FREECAD ASSEMBLY — COMPONENT RECIPES ("70_drawer_box_assembly")

This assembly document has 9 components, labeled P0..P8 below (a component is one placed body or linked part). 0 of them carry a construction recipe — the FreeCAD feature program that regenerates the part from scratch, quoted from this document or its linked companion documents; the rest are supplied as boundary geometry only. No exploded tour is included for this assembly.
COMPONENT P0 — geometry summary ("Body"; no construction recipe available for this part):
  bounding box: 525.0 x 393.0 x 18.0 mm
  tessellated surface: 28 triangles
  volume: 3690964 mm^3 (99% of its bounding box)
  symmetry: mirror-symmetric across its x mid-plane, z mid-plane
COMPONENT P1 — geometry summary ("Body003"; no construction recipe available for this part):
  bounding box: 525.0 x 393.0 x 18.0 mm
  tessellated surface: 28 triangles
  volume: 3690964 mm^3 (99% of its bounding box)
  symmetry: mirror-symmetric across its x mid-plane, z mid-plane
COMPONENT P2 — geometry summary ("Body004"; no construction recipe available for this part):
  bounding box: 771.0 x 378.0 x 18.0 mm
  tessellated surface: 8,124 triangles
  volume: 5203028 mm^3 (99% of its bounding box)
  symmetry: 2-fold rotationally symmetric about the y axis; mirror-symmetric across its x mid-plane
COMPONENT P3 — geometry summary ("Body005"; no construction recipe available for this part):
  bounding box: 771.0 x 378.0 x 18.0 mm
  tessellated surface: 8,124 triangles
  volume: 5203028 mm^3 (99% of its bounding box)
  symmetry: 2-fold rotationally symmetric about the y axis; mirror-symmetric across its x mid-plane
COMPONENT P4 — geometry summary ("Body007"; no construction recipe available for this part):
  bounding box: 489.0 x 101.0 x 18.0 mm
  tessellated surface: 44 triangles
  volume: 844503 mm^3 (95% of its bounding box)
  symmetry: 2-fold rotationally symmetric about the x axis; 2-fold rotationally symmetric about the y axis; 2-fold rotationally symmetric about the z axis; mirror-symmetric across its y mid-plane
COMPONENT P5 — geometry summary ("KV1-45-H45-L...-SC"; no construction recipe available for this part):
  bounding box: 350.0 x 45.0 x 12.7 mm
  tessellated surface: 10,296 triangles
  volume: 86644 mm^3 (43% of its bounding box)
  symmetry: mirror-symmetric across its z mid-plane
COMPONENT P6 — geometry summary ("KV1-45-H45-L...-SC001"; no construction recipe available for this part):
  bounding box: 350.0 x 45.0 x 12.7 mm
  tessellated surface: 10,296 triangles
  volume: 86644 mm^3 (43% of its bounding box)
  symmetry: mirror-symmetric across its z mid-plane
COMPONENT P7 — geometry summary ("KV1-45-H45-L...-SC002"; no construction recipe available for this part):
  bounding box: 350.0 x 45.0 x 12.7 mm
  tessellated surface: 10,296 triangles
  volume: 86644 mm^3 (43% of its bounding box)
  symmetry: mirror-symmetric across its z mid-plane
COMPONENT P8 — geometry summary ("KV1-45-H45-L...-SC003"; no construction recipe available for this part):
  bounding box: 350.0 x 45.0 x 12.7 mm
  tessellated surface: 10,296 triangles
  volume: 86644 mm^3 (43% of its bounding box)
  symmetry: mirror-symmetric across its z mid-plane
PROVENANCE & LICENSES
A FreeCAD (.FCStd) document from a public repository crawl; recipes are the document's own serialized feature recipes (and, for linked parts, companion documents' recipes).
License: as declared in the source repository (recorded in the dataset sidecar).
